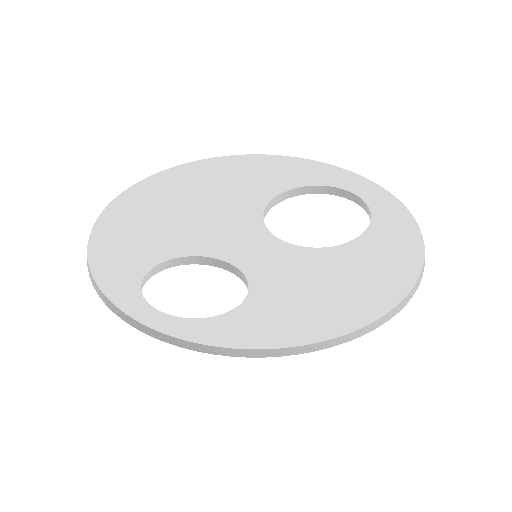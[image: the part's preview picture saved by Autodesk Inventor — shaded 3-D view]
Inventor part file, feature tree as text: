
AUTODESK INVENTOR PART (.ipt)
format: ipt  version: 2025 (Build 290162000, 162)  size: 89,600 bytes
history: native  units: in
note: dims shown in document units (in); Inventor stores cm internally (conversion verified against a paired STEP export)
features: sketch x2, extrude x1
ambient origin geometry x8: Origin, YZ Plane, XZ Plane, XY Plane, X Axis, Y Axis, Z Axis, Center Point
bodies: Solid1 (feature_tree)
feature tree (3):
  sketch  "Sketch1"  dims[d0=2.0in d1=1.0236in]
  extrude  "Extrusion1"  Depth=1.0236in
  sketch  "Sketch2"  dims[d2=0.6378in d3=0.6378in d4=0.0591in d5=0.0in]
